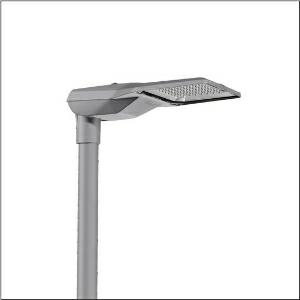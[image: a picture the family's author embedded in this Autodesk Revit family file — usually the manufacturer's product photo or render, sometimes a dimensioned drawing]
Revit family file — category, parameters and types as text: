
# Revit family: streetlight_sl_21_midi___pl52_5xe3h33s08mb_0b8e
name_source: partatom
category: Lighting Fixtures
units: mm (PartAtom-declared; Revit-internal decimal feet)

## family parameters
Cut with Voids When Loaded = No
Host = Face
Light Source = No
Part Type = Normal
Room Calculation Point = No
Round Connector Dimension = Use Diameter
Shared = No

## types (1)
- --- (1 x LED, 17960 lm, 136 W, 3000K)
    Apparent Load = 136 VA
    CIE Flux Codes = 27 59 98 100 100
    Color Rendering = 70
    Color Temperature = 3000K
    Default Elevation = 1800 mm
    Description = Streetlight SL 21 midi, mast luminaire, primary light control with lens, of PMMA, primary optical cover: cover, of toughened safety glass, transparent, light distribution: PL52, light emission: direct distribution, primary light characteristic: asymmetric, installation type: side-entry, post-top, LED, High Power LED, rated luminous flux: 17.960lm, luminous efficacy: 132lm/W, light colour: 730, colour temperature: 3000K, control gear: D4i, control: overheat protection, constant luminous flux control, time-dependent luminous flux control, flexible luminous flux parameterisation, pre-setting: logarithmic dimming characteristic, mains connection: 230..240V, AC, 50/60Hz, start of lifetime: 136W, end of service life: 142W, reduction: 61W, luminaire housing, of diecast aluminium, powder-coated, SITECO metallic grey (DB 702S), corrosivity category C5 high according to DIN EN ISO 12944, please order mast flange separately, inclination adjustable: 0°, 5°, 10°, 15°, sealing non-destructively replaceable, multi-level sealing system, length: 644mm, width: 335mm, height: 110mm, mast flange for spigot size: 42mm (side-entry): 5XC10008XM4, 60/48mm (side-entry/post-top): 5XC10108XM2, 76/60mm (side-entry/post-top): 5XC10108XM1, mounting height: 4..8m, Smart Interface above, protection rating (complete): IP66, insulation class (complete): insulation class II (safety insulation), certification: CE, ENEC, ENEC+, VDE, impact resistance: IK10, permissible operating ambient temperature for outdoor applications: -40..+50°C, standard-compliant lighting for roads and squares, packaging unit: 1 piece

Light Distribution: PL52
    Height = 111 mm
    Lamp = 1 x LED
    Lamp Light Flux = 17960 lm
    Lamp Power = 136 W
    Lamp count = 1
    Length = 644 mm
    Luminous efficacy = 132 lm/W
    Manufacturer = Siteco
    ModVariant = No
    Model = 5XE3H33S08MB
    Number of Poles = 1
    OnlyDefault = Yes
    Power Factor = 1
    Product Name = Streetlight SL 21 midi | PL52
    Product group = mast luminaire | pylon top
    ProductGroupID = 6100
    Protection Class = Protection class II
    Protection Degree = IP 66
    RLX_Detail_Level = 1
    RLX_Emergency_Light_Flux = 0 lm
    RLX_Emergency_Type = 0
    RLX_Emergency_Type_DB = No
    RlxData = <blob elided: 36429 chars, md5=71d316a2>
    Socket = socket
    Standby Power = 0 W
    System Light Flux = 17960 lm
    System Power = 136 W
    Type Comments = factory setting: luminous flux: 100 % | dim-lin: 254 | 695 mA
    Type Image = l_1004302.jpg
    URL = http://relux.com
    VarID = @adj_188129
    Voltage = 0 V
    Weight = 0.00 kg
    Width = 336 mm

## geometry (parser evidence)
native form markers: Blend x4, Sweep x12
no freeform markers — native parametric forms only
